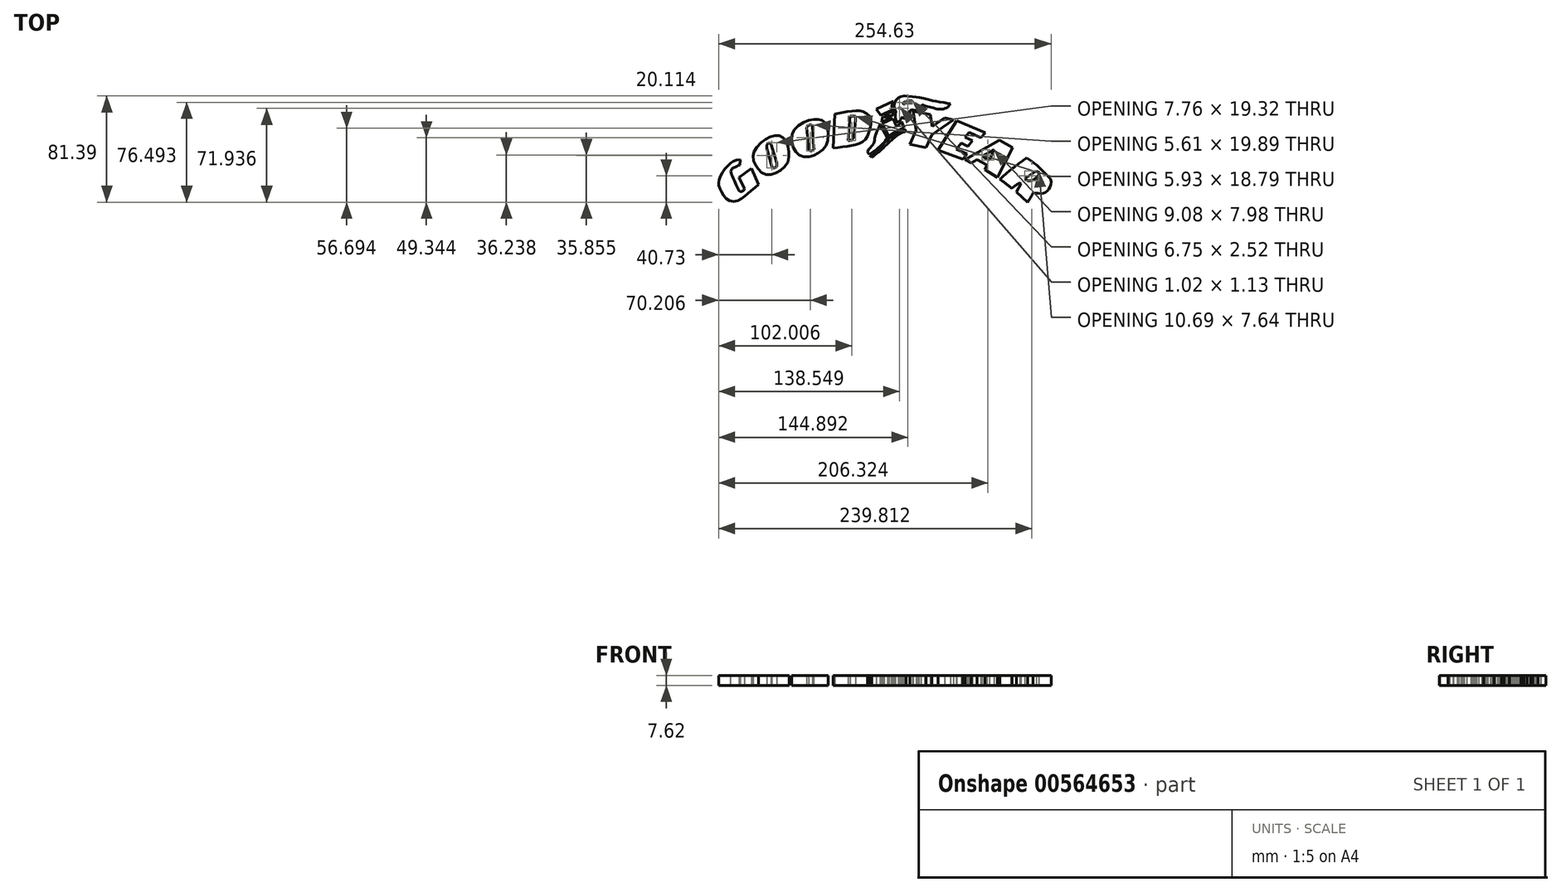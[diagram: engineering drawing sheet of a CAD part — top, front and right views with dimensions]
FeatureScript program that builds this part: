
annotation { "Feature Type Name" : "Feature", "Feature Type Description" : "" }
export const myFeature = defineFeature(function(context is Context, id is Id, definition is map)
    precondition{}
    {
        {
            var Q0;
            Q0=qCreatedBy(makeId("Top.planeOp"),FACE);
            var sketch = newSketch(context, id + "F0", { "sketchPlane" : qUnion([Q0])});
            skFitSpline(sketch, "E0", {"points": [v(-59.77, 19.65) * mm, v(-63.83, 18.9) * mm, v(-66.56, 17.29) * mm, v(-70.08, 14) * mm, v(-73.2, 9.83) * mm, v(-75.73, 4.75) * mm, v(-76.25, 2.47) * mm, v(-76.18, 0) * mm, v(-74.98, -3.55) * mm, v(-72.37, -7.96) * mm, v(-69.17, -11.16) * mm, v(-64.56, -12.56) * mm, v(-59.15, -10.76) * mm, v(-55.35, -7.59) * mm, v(-51.14, -3.95) * mm, v(-45.8, 0.36) * mm], "startDerivative": vector(-48.72, 2.07) * mm, "endDerivative": vector(63.75, 50.3) * mm});
            skLineSegment(sketch, "E1", {"start": v(-59.77, 19.65) * mm, "end": v(-59.86, 15.48) * mm});
            skLineSegment(sketch, "E2", {"start": v(-45.8, 0.36) * mm, "end": v(-51.25, 12.96) * mm});
            skLineSegment(sketch, "E3", {"start": v(-51.25, 12.96) * mm, "end": v(-60.63, 5.88) * mm});
            skLineSegment(sketch, "E4", {"start": v(-60.63, 5.88) * mm, "end": v(-56.41, -2.7) * mm});
            skFitSpline(sketch, "E5", {"points": [v(-59.86, 15.48) * mm, v(-62.4, 14.45) * mm, v(-64.42, 13.43) * mm, v(-66.28, 12.15) * mm, v(-66.87, 9.93) * mm, v(-66.03, 7.47) * mm, v(-64, 2.8) * mm, v(-62.32, -0.84) * mm, v(-61.06, -3.39) * mm, v(-60.55, -4.32) * mm, v(-58.95, -4.91) * mm, v(-57.09, -4.06) * mm, v(-56.41, -2.7) * mm], "startDerivative": vector(-29.78, -11.35) * mm, "endDerivative": vector(6.97, 21.82) * mm});
            skFitSpline(sketch, "E6", {"points": [v(-49.9, 22.3) * mm, v(-48.7, 26.42) * mm, v(-44.08, 32.4) * mm, v(-38.41, 36.27) * mm, v(-33.27, 38.01) * mm, v(-29.32, 37.9) * mm, v(-25.5, 35.12) * mm, v(-23.13, 29.56) * mm, v(-22.34, 23.86) * mm, v(-23.27, 17.75) * mm, v(-27.62, 12.43) * mm, v(-32.9, 9.1) * mm, v(-38.3, 7.89) * mm, v(-43.44, 9.73) * mm, v(-46.87, 13.56) * mm, v(-48.97, 17.14) * mm, v(-49.9, 22.3) * mm]});
            skLineSegment(sketch, "E7", {"start": v(-36.05, 31.72) * mm, "end": v(-31.85, 16.84) * mm});
            skLineSegment(sketch, "E8", {"start": v(-39.36, 28.04) * mm, "end": v(-35.4, 14.58) * mm});
            skFitSpline(sketch, "E9", {"points": [v(-39.36, 28.04) * mm, v(-39.36, 30.3) * mm, v(-38.28, 31.96) * mm, v(-36.88, 32.38) * mm, v(-36.05, 31.72) * mm], "startDerivative": vector(-0.89, 7.93) * mm, "endDerivative": vector(3.61, -4.33) * mm});
            skFitSpline(sketch, "E10", {"points": [v(-31.85, 16.84) * mm, v(-31.85, 14.17) * mm, v(-33.09, 13.34) * mm, v(-34.41, 13.08) * mm, v(-35.4, 14.58) * mm], "startDerivative": vector(1.44, -10.29) * mm, "endDerivative": vector(-1.3, 7.85) * mm});
            skLineSegment(sketch, "E11", {"start": v(-8.9, 44.2) * mm, "end": v(-7.35, 27.45) * mm});
            skLineSegment(sketch, "E12", {"start": v(-4.4, 45.2) * mm, "end": v(-3.4, 28.77) * mm});
            skFitSpline(sketch, "E13", {"points": [v(-8.9, 44.2) * mm, v(-8.13, 45.2) * mm, v(-6.65, 46.05) * mm, v(-5.18, 46.05) * mm, v(-4.4, 45.2) * mm], "startDerivative": vector(2.8, 4.36) * mm, "endDerivative": vector(2.83, -4.51) * mm});
            skFitSpline(sketch, "E14", {"points": [v(-7.35, 27.45) * mm, v(-6.5, 26.52) * mm, v(-5.65, 26.29) * mm, v(-4.64, 26.44) * mm, v(-3.4, 27.3) * mm, v(-3.4, 28.77) * mm], "startDerivative": vector(3.78, -5) * mm, "endDerivative": vector(-0.95, 4.32) * mm});
            skFitSpline(sketch, "E15", {"points": [v(-18.2, 42.64) * mm, v(-12.62, 47.37) * mm, v(-6.27, 49.93) * mm, v(-1.3, 50.4) * mm, v(2.34, 49.85) * mm, v(5.9, 47.3) * mm, v(7.53, 39.7) * mm, v(6.83, 32.33) * mm, v(4.12, 27.53) * mm, v(-1.46, 23.89) * mm, v(-6.11, 21.87) * mm, v(-12.23, 22.1) * mm, v(-16.34, 24.5) * mm, v(-18.82, 28.46) * mm, v(-20.22, 33.88) * mm, v(-19.9, 39.39) * mm, v(-18.2, 42.64) * mm]});
            skLineSegment(sketch, "E16", {"start": v(11.4, 28.26) * mm, "end": v(12.75, 54.33) * mm});
            skFitSpline(sketch, "E17", {"points": [v(12.75, 54.33) * mm, v(20.03, 55.86) * mm, v(28.5, 57.04) * mm, v(34.08, 56.36) * mm, v(39.5, 52.64) * mm, v(40.17, 45.53) * mm, v(38.14, 38.42) * mm, v(34.59, 33.68) * mm, v(28.83, 31.14) * mm, v(21.05, 29.62) * mm, v(11.4, 28.26) * mm], "startDerivative": vector(68.9, 15.11) * mm, "endDerivative": vector(-84.89, -11.4) * mm});
            skLineSegment(sketch, "E18", {"start": v(24.6, 52.98) * mm, "end": v(22.74, 34.19) * mm});
            skFitSpline(sketch, "E19", {"points": [v(24.6, 52.98) * mm, v(27.14, 52.98) * mm, v(28.44, 52.5) * mm, v(28.64, 50.15) * mm, v(27.66, 41.03) * mm, v(26.74, 36.1) * mm, v(26.16, 35.14) * mm, v(25.17, 34.46) * mm, v(22.74, 34.19) * mm], "startDerivative": vector(22.33, 0.87) * mm, "endDerivative": vector(-23, -0.54) * mm});
            skFitSpline(sketch, "E20", {"points": [v(39.1, 23.6) * mm, v(44.18, 27) * mm, v(48.7, 31.12) * mm, v(50.89, 33.22) * mm, v(51.7, 34.88) * mm, v(52.92, 36) * mm], "startDerivative": vector(19.7, 11.7) * mm, "endDerivative": vector(13.38, 3.84) * mm});
            skLineSegment(sketch, "E21", {"start": v(47.46, 46.57) * mm, "end": v(52.92, 36) * mm});
            skFitSpline(sketch, "E22", {"points": [v(47.46, 46.57) * mm, v(46.54, 44.19) * mm, v(45.11, 41.5) * mm, v(43.53, 37) * mm, v(42.43, 32.07) * mm, v(39.8, 28.44) * mm, v(38.07, 26.31) * mm, v(37.96, 24.84) * mm, v(39.1, 23.6) * mm], "startDerivative": vector(-7.2, -21.21) * mm, "endDerivative": vector(15.31, -12.42) * mm});
            skLineSegment(sketch, "E23", {"start": v(40.96, 21.31) * mm, "end": v(39.53, 22.69) * mm});
            skLineSegment(sketch, "E24", {"start": v(65.88, 43.08) * mm, "end": v(67.2, 41.3) * mm});
            skFitSpline(sketch, "E25", {"points": [v(65.88, 43.08) * mm, v(64.37, 42.22) * mm, v(62.42, 41.22) * mm, v(59.63, 39.5) * mm, v(56.94, 37.62) * mm, v(53.71, 35.18) * mm, v(48.96, 30.47) * mm, v(47.97, 29.32) * mm, v(46.11, 27.54) * mm, v(43.82, 25.45) * mm, v(41.44, 24.06) * mm, v(39.53, 22.69) * mm], "startDerivative": vector(-17.38, -20) * mm, "endDerivative": vector(-22.35, -17.46) * mm});
            skFitSpline(sketch, "E26", {"points": [v(67.2, 41.3) * mm, v(66, 40.84) * mm, v(64.5, 40.51) * mm, v(62.4, 39.36) * mm, v(58.05, 36.12) * mm, v(53.94, 32.64) * mm, v(49.63, 28.21) * mm, v(46.94, 25.96) * mm, v(44.17, 23.59) * mm, v(40.96, 21.31) * mm], "startDerivative": vector(-16.72, -16.2) * mm, "endDerivative": vector(-28.08, -18.76) * mm});
            skLineSegment(sketch, "E27", {"start": v(47.81, 53.38) * mm, "end": v(44.5, 58.28) * mm});
            skLineSegment(sketch, "E28", {"start": v(44.5, 58.28) * mm, "end": v(57.43, 64.4) * mm});
            skLineSegment(sketch, "E29", {"start": v(47.81, 53.38) * mm, "end": v(57.06, 57.79) * mm});
            skFitSpline(sketch, "E30", {"points": [v(57.43, 64.4) * mm, v(56.51, 62.01) * mm, v(56.51, 59.2) * mm, v(57.06, 57.79) * mm], "startDerivative": vector(-3.12, -6.33) * mm, "endDerivative": vector(2.33, -4.57) * mm});
            skLineSegment(sketch, "E31", {"start": v(50.63, 53.74) * mm, "end": v(57.69, 57.09) * mm});
            skLineSegment(sketch, "E32", {"start": v(50.63, 53.74) * mm, "end": v(57.3, 53.2) * mm});
            skFitSpline(sketch, "E33", {"points": [v(57.69, 57.09) * mm, v(57.17, 55.72) * mm, v(57.3, 53.2) * mm], "startDerivative": vector(-2.15, -4.28) * mm, "endDerivative": vector(1.5, -3.48) * mm});
            skLineSegment(sketch, "E34", {"start": v(48.55, 48.32) * mm, "end": v(49.17, 52.19) * mm});
            skLineSegment(sketch, "E35", {"start": v(49.17, 52.19) * mm, "end": v(56.3, 51.91) * mm});
            skLineSegment(sketch, "E36", {"start": v(48.55, 48.32) * mm, "end": v(56.3, 51.91) * mm});
            skLineSegment(sketch, "E37", {"start": v(48.94, 47.29) * mm, "end": v(54.3, 36.9) * mm});
            skLineSegment(sketch, "E38", {"start": v(48.94, 47.29) * mm, "end": v(57.19, 51.08) * mm});
            skLineSegment(sketch, "E39", {"start": v(57.19, 51.08) * mm, "end": v(58.36, 48.52) * mm});
            skFitSpline(sketch, "E40", {"points": [v(58.36, 48.52) * mm, v(59.08, 46.84) * mm, v(59.66, 45.79) * mm, v(61.14, 45.98) * mm, v(63.83, 48.86) * mm], "startDerivative": vector(3.27, -7.15) * mm, "endDerivative": vector(7.57, 10.06) * mm});
            skLineSegment(sketch, "E41", {"start": v(63.83, 48.86) * mm, "end": v(65.82, 44.11) * mm});
            skFitSpline(sketch, "E42", {"points": [v(54.3, 36.9) * mm, v(55.69, 38.57) * mm, v(60.65, 41.48) * mm, v(65.82, 44.11) * mm], "startDerivative": vector(4.45, 7) * mm, "endDerivative": vector(13.02, 6.62) * mm});
            skFitSpline(sketch, "E43", {"points": [v(61.18, 48.14) * mm, v(59.75, 49.36) * mm, v(58.81, 53.55) * mm, v(59.36, 56.2) * mm, v(58.43, 58.46) * mm, v(58.43, 62.76) * mm, v(60.3, 66.01) * mm, v(63.28, 67.89) * mm, v(68.08, 68.22) * mm, v(73.92, 67.61) * mm, v(78.94, 66.95) * mm, v(86.83, 64.74) * mm, v(91.57, 63.97) * mm, v(97.08, 63.03) * mm, v(101.33, 62.43) * mm], "startDerivative": vector(-31.99, 17.8) * mm, "endDerivative": vector(56.5, -7.36) * mm});
            skFitSpline(sketch, "E44", {"points": [v(101.33, 62.43) * mm, v(98.46, 59.34) * mm, v(94.1, 58.18) * mm, v(88.87, 58.9) * mm, v(84.12, 60.28) * mm, v(81.15, 61.1) * mm, v(79.88, 61.54) * mm, v(79.16, 60.94) * mm, v(79.71, 60.39) * mm, v(80.65, 59.9) * mm, v(81.75, 59.72) * mm], "startDerivative": vector(-19.3, -26.52) * mm, "endDerivative": vector(16.87, -1.16) * mm});
            skFitSpline(sketch, "E45", {"points": [v(81.75, 59.72) * mm, v(79.88, 58.68) * mm, v(78, 58.73) * mm, v(76.46, 58.95) * mm, v(76.4, 58.24) * mm, v(77.18, 57.85) * mm], "startDerivative": vector(-7.43, -5.2) * mm, "endDerivative": vector(5.92, -1.38) * mm});
            skFitSpline(sketch, "E46", {"points": [v(77.18, 57.85) * mm, v(76.35, 57.32) * mm, v(74.43, 57.29) * mm, v(72.68, 57.62) * mm, v(70.63, 57.45) * mm, v(70.2, 54.94) * mm, v(69.4, 53.45) * mm, v(67.58, 53.5) * mm, v(66.48, 51.67) * mm, v(65.59, 51) * mm, v(64.36, 51.84) * mm, v(63.05, 50.4) * mm, v(62.37, 48.62) * mm, v(61.18, 48.14) * mm], "startDerivative": vector(-11.9, -10.87) * mm, "endDerivative": vector(-16.98, 9.93) * mm});
            skFitSpline(sketch, "E47", {"points": [v(61.74, 59.24) * mm, v(62.63, 59.24) * mm, v(62.65, 58.37) * mm, v(62.19, 58.35) * mm, v(62.32, 58.84) * mm, v(61.9, 58.82) * mm, v(61.74, 59.24) * mm]});
            skFitSpline(sketch, "E48", {"points": [v(65.21, 62.9) * mm, v(66.4, 63.76) * mm, v(68.44, 64.34) * mm, v(70.3, 64.56) * mm, v(71.94, 64.47) * mm, v(71.87, 63.65) * mm, v(69.29, 63.25) * mm, v(66.9, 62.78) * mm, v(66.02, 62.18) * mm, v(65.15, 62.25) * mm, v(65.21, 62.9) * mm]});
            skLineSegment(sketch, "E49", {"start": v(72.66, 56.7) * mm, "end": v(75.06, 41.97) * mm});
            skLineSegment(sketch, "E50", {"start": v(75.06, 41.97) * mm, "end": v(70.23, 31.2) * mm});
            skLineSegment(sketch, "E51", {"start": v(70.23, 31.2) * mm, "end": v(82.54, 28.69) * mm});
            skLineSegment(sketch, "E52", {"start": v(82.54, 28.69) * mm, "end": v(87, 38.62) * mm});
            skLineSegment(sketch, "E53", {"start": v(87, 38.62) * mm, "end": v(103.68, 50.06) * mm});
            skLineSegment(sketch, "E54", {"start": v(103.68, 50.06) * mm, "end": v(96.8, 51.47) * mm});
            skLineSegment(sketch, "E55", {"start": v(96.8, 51.47) * mm, "end": v(87.33, 44.97) * mm});
            skLineSegment(sketch, "E56", {"start": v(87.33, 44.97) * mm, "end": v(85.86, 54) * mm});
            skLineSegment(sketch, "E57", {"start": v(85.86, 54) * mm, "end": v(72.66, 56.7) * mm});
            skLineSegment(sketch, "E58", {"start": v(91.9, 26.82) * mm, "end": v(106.1, 49.42) * mm});
            skLineSegment(sketch, "E59", {"start": v(106.1, 49.42) * mm, "end": v(128.08, 40.3) * mm});
            skLineSegment(sketch, "E60", {"start": v(128.08, 40.3) * mm, "end": v(124.49, 36.46) * mm});
            skLineSegment(sketch, "E61", {"start": v(124.49, 36.46) * mm, "end": v(115.55, 40.57) * mm});
            skLineSegment(sketch, "E62", {"start": v(115.55, 40.57) * mm, "end": v(112.49, 36.8) * mm});
            skLineSegment(sketch, "E63", {"start": v(112.49, 36.8) * mm, "end": v(118.1, 34.18) * mm});
            skLineSegment(sketch, "E64", {"start": v(118.1, 34.18) * mm, "end": v(114.68, 29.54) * mm});
            skLineSegment(sketch, "E65", {"start": v(114.68, 29.54) * mm, "end": v(109.42, 32.16) * mm});
            skLineSegment(sketch, "E66", {"start": v(109.42, 32.16) * mm, "end": v(105.74, 27.43) * mm});
            skLineSegment(sketch, "E67", {"start": v(105.74, 27.43) * mm, "end": v(114.15, 24.02) * mm});
            skLineSegment(sketch, "E68", {"start": v(114.15, 24.02) * mm, "end": v(110.82, 20) * mm});
            skLineSegment(sketch, "E69", {"start": v(110.82, 20) * mm, "end": v(91.9, 26.82) * mm});
            skLineSegment(sketch, "E70", {"start": v(112.29, 19.53) * mm, "end": v(138.65, 34.6) * mm});
            skLineSegment(sketch, "E71", {"start": v(138.65, 34.6) * mm, "end": v(149.02, 28.7) * mm});
            skLineSegment(sketch, "E72", {"start": v(149.02, 28.7) * mm, "end": v(137.16, 5.95) * mm});
            skLineSegment(sketch, "E73", {"start": v(137.16, 5.95) * mm, "end": v(127.55, 11.85) * mm});
            skLineSegment(sketch, "E74", {"start": v(127.55, 11.85) * mm, "end": v(129.33, 15.35) * mm});
            skLineSegment(sketch, "E75", {"start": v(129.33, 15.35) * mm, "end": v(121.52, 19.59) * mm});
            skLineSegment(sketch, "E76", {"start": v(121.52, 19.59) * mm, "end": v(117.2, 16.87) * mm});
            skLineSegment(sketch, "E77", {"start": v(117.2, 16.87) * mm, "end": v(112.29, 19.53) * mm});
            skLineSegment(sketch, "E78", {"start": v(125.49, 22.15) * mm, "end": v(134.56, 27.12) * mm});
            skLineSegment(sketch, "E79", {"start": v(134.56, 27.12) * mm, "end": v(131.04, 19.14) * mm});
            skLineSegment(sketch, "E80", {"start": v(131.04, 19.14) * mm, "end": v(125.49, 22.15) * mm});
            skFitSpline(sketch, "E81", {"points": [v(139.14, 4.57) * mm, v(145.18, 9.89) * mm, v(153.62, 16.45) * mm, v(159.77, 20.93) * mm], "startDerivative": vector(17.67, 16.08) * mm, "endDerivative": vector(18.73, 13.48) * mm});
            skFitSpline(sketch, "E82", {"points": [v(159.77, 20.93) * mm, v(168.42, 14.37) * mm, v(174.98, 7.8) * mm, v(178.1, 3.84) * mm, v(177.07, -2.4) * mm, v(172.06, -6.16) * mm, v(164.56, -5.74) * mm], "startDerivative": vector(44.5, -30.97) * mm, "endDerivative": vector(-46.73, 8.55) * mm});
            skFitSpline(sketch, "E83", {"points": [v(164.56, -5.74) * mm, v(162.69, -9.4) * mm, v(160.38, -13.1) * mm], "startDerivative": vector(-3.62, -7.3) * mm, "endDerivative": vector(-4.1, -6.66) * mm});
            skFitSpline(sketch, "E84", {"points": [v(139.14, 4.57) * mm, v(143.4, 1.34) * mm, v(148.2, -2.4) * mm], "startDerivative": vector(8.71, -6.53) * mm, "endDerivative": vector(9.4, -7.42) * mm});
            skFitSpline(sketch, "E85", {"points": [v(148.2, -2.4) * mm, v(150.73, -0.48) * mm, v(154.35, 1.86) * mm], "startDerivative": vector(4.88, 2.85) * mm, "endDerivative": vector(7.3, 5.55) * mm});
            skLineSegment(sketch, "E86", {"start": v(154.35, 1.86) * mm, "end": v(155.3, 1.04) * mm});
            skLineSegment(sketch, "E87", {"start": v(155.3, 1.04) * mm, "end": v(151.65, -5.27) * mm});
            skLineSegment(sketch, "E88", {"start": v(151.65, -5.27) * mm, "end": v(160.38, -13.1) * mm});
            skLineSegment(sketch, "E89", {"start": v(158.17, 4.93) * mm, "end": v(167, 10.82) * mm});
            skFitSpline(sketch, "E90", {"points": [v(167, 10.82) * mm, v(168.9, 9.08) * mm, v(167.83, 6.42) * mm, v(164.02, 3.8) * mm, v(161.31, 3.23) * mm, v(158.17, 4.93) * mm], "startDerivative": vector(14.19, -8.55) * mm, "endDerivative": vector(-15.28, 10.77) * mm});
            skSolve(sketch);
        }
        {
            var Q0;
            Q0=qSketchRegion(id+"F0",true);
            extrude(context, id + "F1", {"entities" : qUnion([Q0]), "depth" : 7.62 * mm, "offsetDistance" : 25.4 * mm});
        }
    });
